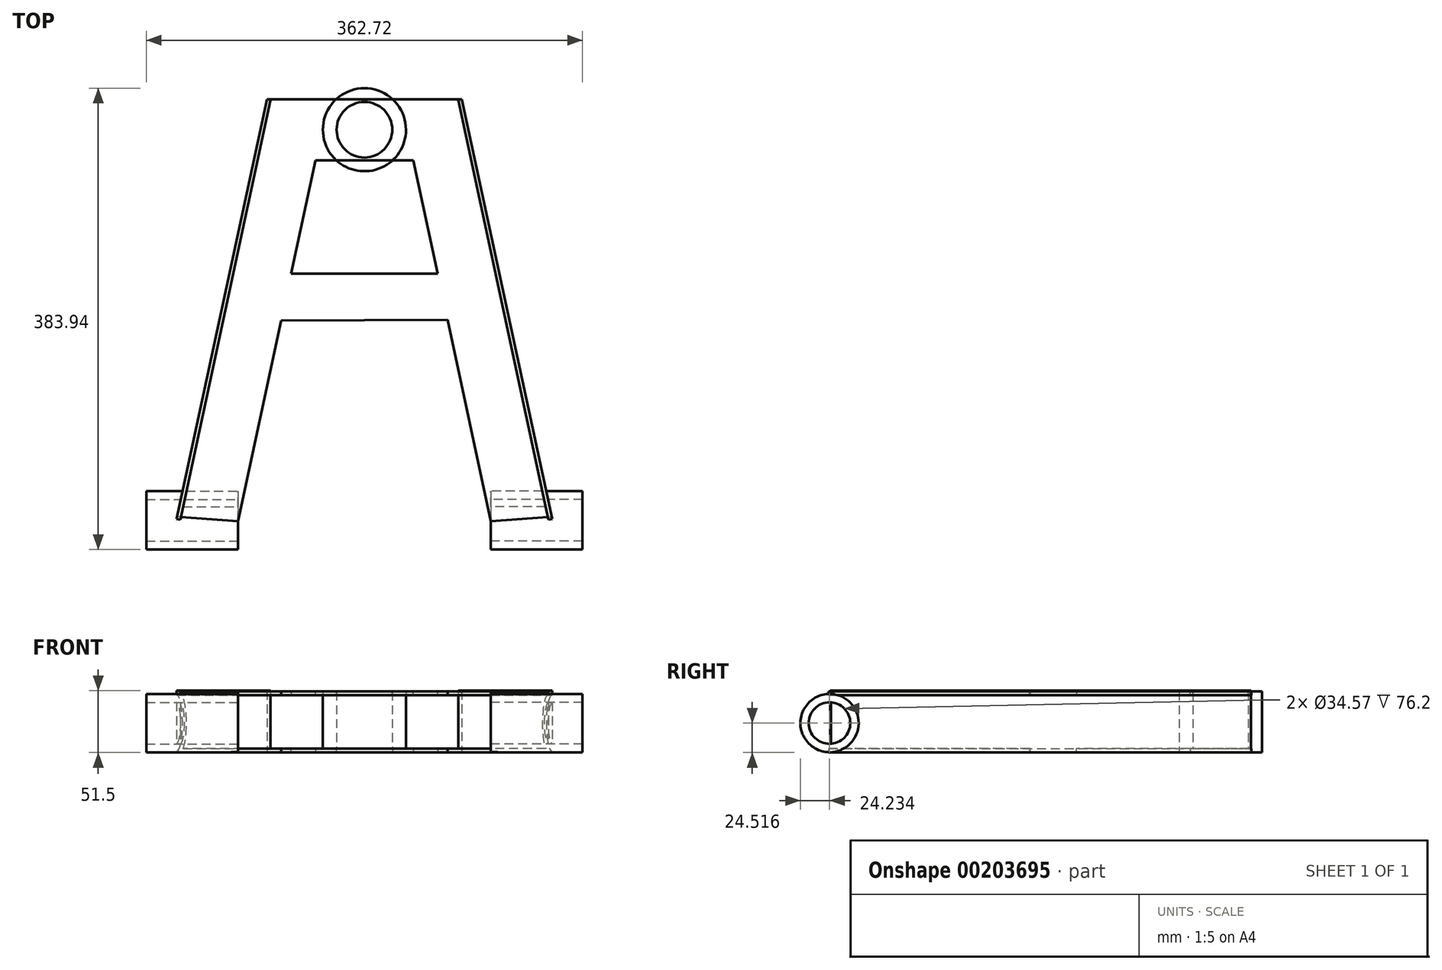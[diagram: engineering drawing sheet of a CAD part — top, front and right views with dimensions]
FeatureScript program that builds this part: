
annotation { "Feature Type Name" : "Feature", "Feature Type Description" : "" }
export const myFeature = defineFeature(function(context is Context, id is Id, definition is map)
    precondition{}
    {
        {
            var Q0;
            Q0=qCreatedBy(makeId("Top.planeOp"),FACE);
            var sketch = newSketch(context, id + "F15", { "sketchPlane" : qUnion([Q0])});
            skLineSegment(sketch, "E0", {"start": v(-155.83, -92.94) * mm, "end": v(-81.04, 254.7) * mm});
            skLineSegment(sketch, "E1", {"start": v(-81.04, 254.7) * mm, "end": v(0, 254.7) * mm});
            skLineSegment(sketch, "E2", {"start": v(0, 254.7) * mm, "end": v(0, 203.9) * mm});
            skLineSegment(sketch, "E3", {"start": v(0, 203.9) * mm, "end": v(-40.52, 203.9) * mm});
            skPoint(sketch, "E3.endSnap0", {"position": v(-40.52, 254.7) * mm});
            skLineSegment(sketch, "E4", {"start": v(-40.52, 203.9) * mm, "end": v(-105.16, -96.54) * mm});
            skLineSegment(sketch, "E5", {"start": v(-105.16, -96.54) * mm, "end": v(-155.83, -92.94) * mm});
            skSolve(sketch);
        }
        {
            var Q0;
            Q0=makeQuery(id+"F15.imprint","IMPRINT",FACE,{"disambiguationData":[TD([[makeQuery(id+"F15.imprint","IMPRINT",EDGE,{"derivedFrom":sQuery(id+"F15.wireOp",EDGE,"E0")}),-1.0]])]});
            var sketch = newSketch(context, id + "F0", { "sketchPlane" : qUnion([Q0])});
            skSolve(sketch);
        }
        {
            var Q0;
            Q0=makeQuery(id+"F0.imprint","IMPRINT",FACE,{"disambiguationData":[TD([[makeQuery(id+"F0.imprint","IMPRINT",EDGE,{"derivedFrom":makeQuery(id+"F15.imprint","IMPRINT",EDGE,{"derivedFrom":sQuery(id+"F15.wireOp",EDGE,"E0")})}),-1.0]])]});
            var sketch = newSketch(context, id + "F16", { "sketchPlane" : qUnion([Q0])});
            skSolve(sketch);
        }
        {
            var Q0;
            Q0 = qSketchRegion(id + "F16", true);
            var Q1;
            Q1=makeQuery(id+"F0.imprint","IMPRINT",FACE,{"disambiguationData":[TD([[makeQuery(id+"F0.imprint","IMPRINT",EDGE,{"derivedFrom":makeQuery(id+"F15.imprint","IMPRINT",EDGE,{"derivedFrom":sQuery(id+"F15.wireOp",EDGE,"E0")})}),-1.0]])]});
            extrude(context, id + "F1", {"entities" : qUnion([Q0, Q1]), "depth" : 3.17 * mm});
        }
        {
            var Q0;
            Q0=makeQuery(id+"F1.opExtrude","SWEPT_BODY",BODY,{"disambiguationData":[OSD([sQuery(id+"F15.wireOp",EDGE,"E0"),sQuery(id+"F15.wireOp",EDGE,"E1"),sQuery(id+"F15.wireOp",EDGE,"E2"),sQuery(id+"F15.wireOp",EDGE,"E3"),sQuery(id+"F15.wireOp",EDGE,"E4"),sQuery(id+"F15.wireOp",EDGE,"E5")])]});
            var Q1;
            Q1=qCreatedBy(makeId("Right.planeOp"),FACE);
            mirror(context, id + "F2", {"operationType" : NewBodyOperationType.ADD, "entities" : qUnion([Q0]), "mirrorPlane" : qUnion([Q1])});
        }
        {
            var Q0;
            Q0=qCreatedBy(makeId("Top.planeOp"),FACE);
            var sketch = newSketch(context, id + "F17", { "sketchPlane" : qUnion([Q0])});
            skLineSegment(sketch, "E6", {"start": v(-71.31, 109.48) * mm, "end": v(64.14, 109.48) * mm});
            skLineSegment(sketch, "E7", {"start": v(64.14, 109.48) * mm, "end": v(86.4, 71.08) * mm});
            skLineSegment(sketch, "E8", {"start": v(86.4, 71.08) * mm, "end": v(-85.48, 70.33) * mm});
            skLineSegment(sketch, "E9", {"start": v(-85.48, 70.33) * mm, "end": v(-71.31, 109.48) * mm});
            skSolve(sketch);
        }
        {
            var Q0;
            Q0=makeQuery(id+"F17.imprint","IMPRINT",FACE,{"disambiguationData":[TD([[makeQuery(id+"F17.imprint","IMPRINT",EDGE,{"derivedFrom":sQuery(id+"F17.wireOp",EDGE,"E6")}),-1.0]])]});
            extrude(context, id + "F3", {"entities" : qUnion([Q0]), "operationType" : NewBodyOperationType.ADD, "depth" : 3.17 * mm});
        }
        {
            var Q0;
            Q0=qCreatedBy(makeId("Top.planeOp"),FACE);
            cPlane(context, id + "F4", {"entities" : qUnion([Q0]), "cplaneType" : CPlaneType.OFFSET, "offset" : 25.4 * mm, "width" : 152.4 * mm, "height" : 152.4 * mm});
        }
        {
            var Q0;
            Q0=sQuery(id+"F15.wireOp",BODY,"E4");
            var Q1;
            Q1=makeQuery(id+"F1.opExtrude","SWEPT_BODY",BODY,{"disambiguationData":[OSD([sQuery(id+"F15.wireOp",EDGE,"E0"),sQuery(id+"F15.wireOp",EDGE,"E1"),sQuery(id+"F15.wireOp",EDGE,"E2"),sQuery(id+"F15.wireOp",EDGE,"E3"),sQuery(id+"F15.wireOp",EDGE,"E4"),sQuery(id+"F15.wireOp",EDGE,"E5")])]});
            var Q2;
            Q2=qCreatedBy(id+"F4.planeOp",FACE);
            mirror(context, id + "F5", {"entities" : qUnion([Q0, Q1]), "mirrorPlane" : qUnion([Q2])});
        }
        {
            var Q0;
            Q0=makeQuery(id+"F5.opPattern","COPY",VERTEX,{"derivedFrom":makeQuery(id+"F1.opExtrude","CAP_VERTEX",VERTEX,{"disambiguationData":[OSD([sQuery(id+"F15.wireOp",EDGE,"E0"),sQuery(id+"F15.wireOp",EDGE,"E1")])],"isStart":true}),"instanceName":"1"});
            var Q1;
            Q1=makeQuery(id+"F1.opExtrude","CAP_VERTEX",VERTEX,{"disambiguationData":[OSD([sQuery(id+"F15.wireOp",EDGE,"E0"),sQuery(id+"F15.wireOp",EDGE,"E1")])],"isStart":false});
            var Q2;
            Q2=makeQuery(id+"F5.opPattern","COPY",VERTEX,{"derivedFrom":makeQuery(id+"F1.opExtrude","CAP_VERTEX",VERTEX,{"disambiguationData":[OSD([sQuery(id+"F15.wireOp",EDGE,"E0"),sQuery(id+"F15.wireOp",EDGE,"E5")])],"isStart":false}),"instanceName":"1"});
            cPlane(context, id + "F6", {"entities" : qUnion([Q0, Q1, Q2]), "cplaneType" : CPlaneType.THREE_POINT, "offset" : 25.4 * mm, "width" : 152.4 * mm, "height" : 152.4 * mm});
        }
        {
            var Q0;
            Q0=qCreatedBy(id+"F6.planeOp",FACE);
            var sketch = newSketch(context, id + "F7", { "sketchPlane" : qUnion([Q0])});
            skLineSegment(sketch, "E10.bottom", {"start": v(231.72, 51.5) * mm, "end": v(-125.37, 51.5) * mm});
            skLineSegment(sketch, "E10.top", {"start": v(231.72, 0) * mm, "end": v(-125.37, 0) * mm});
            skLineSegment(sketch, "E10.left", {"start": v(231.72, 51.5) * mm, "end": v(231.72, 0) * mm});
            skLineSegment(sketch, "E10.right", {"start": v(-125.37, 51.5) * mm, "end": v(-125.37, 0) * mm});
            skSolve(sketch);
        }
        {
            var Q0;
            Q0 = qSketchRegion(id + "F7", true);
            extrude(context, id + "F8", {"entities" : qUnion([Q0]), "depth" : 3.17 * mm});
        }
        {
            var Q0;
            Q0=makeQuery(id+"F8.opExtrude","SWEPT_BODY",BODY,{"disambiguationData":[OSD([sQuery(id+"F7.wireOp",EDGE,"E10.bottom"),sQuery(id+"F7.wireOp",EDGE,"E10.top"),sQuery(id+"F7.wireOp",EDGE,"E10.left"),sQuery(id+"F7.wireOp",EDGE,"E10.right")])]});
            var Q1;
            Q1=qCreatedBy(makeId("Right.planeOp"),FACE);
            mirror(context, id + "F18", {"entities" : qUnion([Q0]), "mirrorPlane" : qUnion([Q1])});
        }
        {
            var Q0;
            Q0=qCreatedBy(makeId("Right.planeOp"),FACE);
            var Q1;
            Q1=makeQuery(id+"F2.opPattern","COPY",VERTEX,{"derivedFrom":makeQuery(id+"F1.opExtrude","CAP_VERTEX",VERTEX,{"disambiguationData":[OSD([sQuery(id+"F15.wireOp",EDGE,"E4"),sQuery(id+"F15.wireOp",EDGE,"E5")])],"isStart":false}),"instanceName":"1"});
            cPlane(context, id + "F9", {"entities" : qUnion([Q0, Q1]), "cplaneType" : CPlaneType.PLANE_POINT, "offset" : 25.4 * mm, "width" : 152.4 * mm, "height" : 152.4 * mm});
        }
        {
            var Q0;
            Q0=qCreatedBy(id+"F9.planeOp",FACE);
            var sketch = newSketch(context, id + "F10", { "sketchPlane" : qUnion([Q0])});
            skCircle(sketch, "E11", {"center": v(-95.9, 24.52) * mm, "radius": 24.24 * mm});
            skCircle(sketch, "E12", {"center": v(-95.9, 24.52) * mm, "radius": 17.28 * mm});
            skSolve(sketch);
        }
        {
            var Q0;
            Q0 = qSketchRegion(id + "F10", true);
            extrude(context, id + "F19", {"entities" : qUnion([Q0]), "depth" : 76.2 * mm});
        }
        {
            var Q0;
            Q0=makeQuery(id+"F19.opExtrude","SWEPT_BODY",BODY,{"disambiguationData":[OSD([sQuery(id+"F10.wireOp",EDGE,"E11"),sQuery(id+"F10.wireOp",EDGE,"E12")])]});
            var Q1;
            Q1=qCreatedBy(makeId("Right.planeOp"),FACE);
            mirror(context, id + "F11", {"entities" : qUnion([Q0]), "mirrorPlane" : qUnion([Q1])});
        }
        {
            var Q0;
            Q0=qCreatedBy(makeId("Top.planeOp"),FACE);
            var sketch = newSketch(context, id + "F20", { "sketchPlane" : qUnion([Q0])});
            skCircle(sketch, "E13", {"center": v(0, 229.25) * mm, "radius": 34.56 * mm});
            skCircle(sketch, "E14", {"center": v(0, 229.25) * mm, "radius": 23.13 * mm});
            skSolve(sketch);
        }
        {
            var Q0;
            Q0=makeQuery(id+"F20.imprint","IMPRINT",FACE,{"disambiguationData":[TD([[makeQuery(id+"F20.imprint","IMPRINT",EDGE,{"derivedFrom":sQuery(id+"F20.wireOp",EDGE,"E13")}),1.0]])]});
            var Q1;
            Q1=sQuery(id+"F20.wireOp",EDGE,"E14");
            var Q2;
            Q2=sQuery(id+"F20.wireOp",EDGE,"E13");
            extrude(context, id + "F12", {"entities" : qUnion([Q0]), "surfaceEntities" : qUnion([Q1, Q2]), "depth" : 50.8 * mm});
        }
        {
            var Q0;
            Q0=makeQuery(id+"F20.imprint","IMPRINT",FACE,{"disambiguationData":[TD([[makeQuery(id+"F20.imprint","IMPRINT",EDGE,{"derivedFrom":sQuery(id+"F20.wireOp",EDGE,"E14")}),1.0]])]});
            extrude(context, id + "F21", {"entities" : qUnion([Q0]), "operationType" : NewBodyOperationType.REMOVE, "endBound" : BoundingType.SYMMETRIC, "oppositeDirection" : true, "depth" : 127 * mm});
        }
        {
            var Q0;
            Q0=makeQuery(id+"F15.imprint","IMPRINT",FACE,{"disambiguationData":[TD([[makeQuery(id+"F15.imprint","IMPRINT",EDGE,{"derivedFrom":sQuery(id+"F15.wireOp",EDGE,"E0")}),-1.0]])]});
            extrude(context, id + "F13", {"entities" : qUnion([Q0]), "depth" : 3.17 * mm});
        }
        {
            var Q0;
            Q0=makeQuery(id+"F13.opExtrude","SWEPT_BODY",BODY,{"disambiguationData":[OSD([sQuery(id+"F15.wireOp",EDGE,"E0"),sQuery(id+"F15.wireOp",EDGE,"E1"),sQuery(id+"F15.wireOp",EDGE,"E2"),sQuery(id+"F15.wireOp",EDGE,"E3"),sQuery(id+"F15.wireOp",EDGE,"E4"),sQuery(id+"F15.wireOp",EDGE,"E5")])]});
            var Q1;
            Q1=qCreatedBy(makeId("Right.planeOp"),FACE);
            mirror(context, id + "F14", {"operationType" : NewBodyOperationType.ADD, "entities" : qUnion([Q0]), "mirrorPlane" : qUnion([Q1])});
        }
    });
